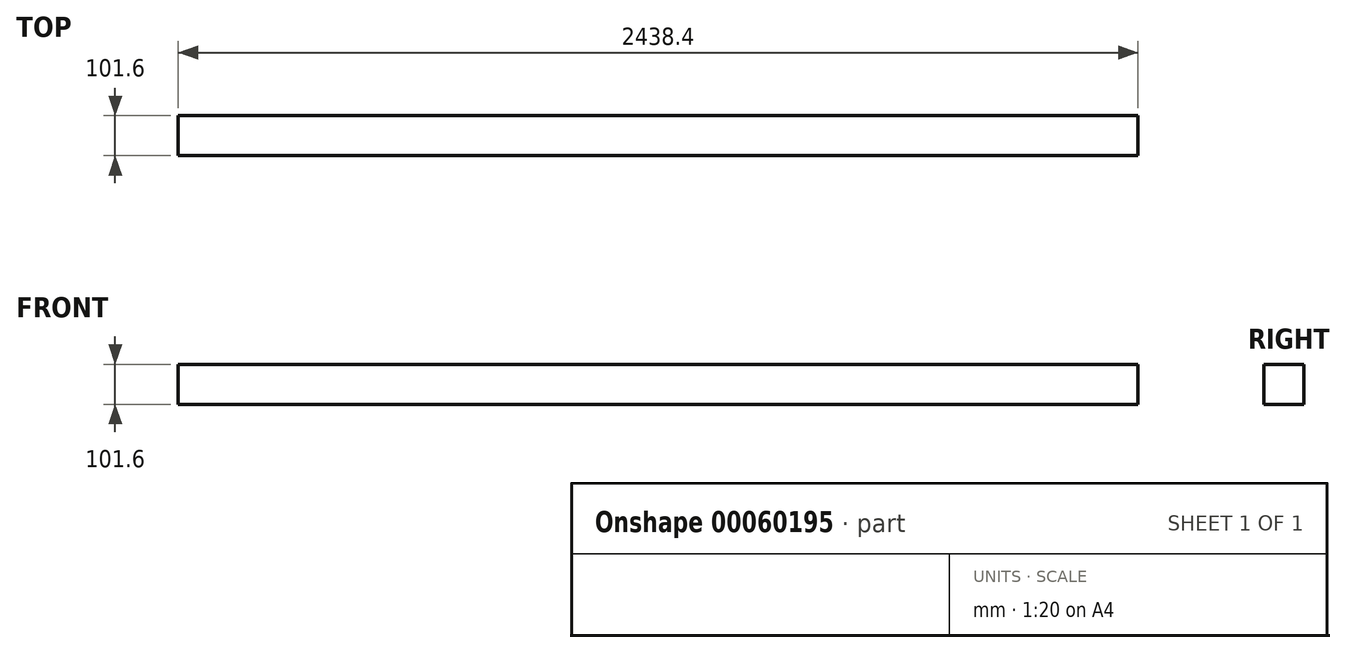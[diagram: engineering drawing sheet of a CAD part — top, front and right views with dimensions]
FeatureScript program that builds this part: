
annotation { "Feature Type Name" : "Feature", "Feature Type Description" : "" }
export const myFeature = defineFeature(function(context is Context, id is Id, definition is map)
    precondition{}
    {
        {
            var Q0;
            Q0=qCreatedBy(makeId("Right.planeOp"),FACE);
            var sketch = newSketch(context, id + "F0", { "sketchPlane" : qUnion([Q0])});
            skLineSegment(sketch, "E0.rect.bottom", {"start": v(50.8, 50.8) * mm, "end": v(-50.8, 50.8) * mm});
            skLineSegment(sketch, "E0.rect.top", {"start": v(50.8, -50.8) * mm, "end": v(-50.8, -50.8) * mm});
            skLineSegment(sketch, "E0.rect.left", {"start": v(50.8, 50.8) * mm, "end": v(50.8, -50.8) * mm});
            skLineSegment(sketch, "E0.rect.right", {"start": v(-50.8, 50.8) * mm, "end": v(-50.8, -50.8) * mm});
            skPoint(sketch, "E0.rect.middle", {"position": v(0, 0) * mm});
            skSolve(sketch);
        }
        {
            var Q0;
            Q0 = qSketchRegion(id + "F0", true);
            extrude(context, id + "F1", {"entities" : qUnion([Q0]), "depth" : 2438.4 * mm});
        }
    });
